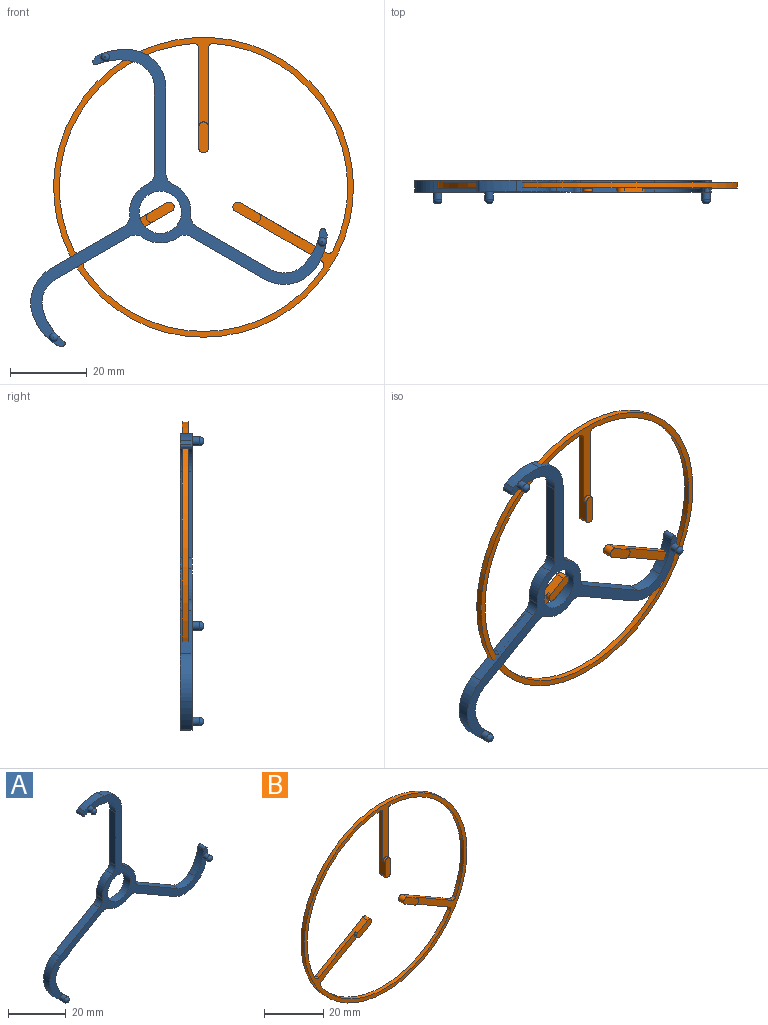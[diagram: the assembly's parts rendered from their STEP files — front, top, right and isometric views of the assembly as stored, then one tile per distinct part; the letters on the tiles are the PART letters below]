
ASSEMBLY  parts=2 mates=1
PART A: 48 faces, bbox 77.2x6x77.2 mm
  f0: plane 3.69x2.41mm, normal (0,-1,0), area 4.6mm2, adj f12,f13,f14,f25,f43
  f1: plane 76.92x75.78mm, normal (0,-1,0), area 488.1mm2, adj f3,f4,f5,f6,f8,f9,f10,f11
  f2: plane 3.75x3.07mm, normal (0,-1,0), area 4.6mm2, adj f6,f7,f8,f26,f41
  f3: plane 22.3x3mm, normal (-1,0,0), area 66.9mm2, adj f1,f23,f30,f33
  f4: cylinder r=8mm len=8.12mm, axis (0,1,0), area 30mm2, adj f1,f23,f33,f38
  f5: plane 19.27x11.13mm, normal (-0.5,0,0.87), area 66.8mm2, adj f1,f23,f29,f38
  f6: cylinder r=16mm len=7.37mm, axis (0,1,0), area 29.4mm2, adj f1,f2,f7,f23,f29
  f7: plane 3x1.13mm, normal (-0.13,0,-0.99), area 3.4mm2, adj f2,f6,f23,f26
  f8: cylinder r=15mm len=8.27mm, axis (0,1,0), area 30.4mm2, adj f1,f2,f23,f26,f32
  f9: plane 19.32x11.15mm, normal (0.5,0,-0.87), area 66.9mm2, adj f1,f23,f32,f37
  f10: cylinder r=8mm len=9.37mm, axis (0,1,0), area 30mm2, adj f1,f23,f36,f37
  f11: plane 19.27x11.13mm, normal (-0.5,0,-0.87), area 66.8mm2, adj f1,f23,f28,f36
  f12: cylinder r=16mm len=9.08mm, axis (0,1,0), area 29.4mm2, adj f0,f1,f13,f23,f28
  f13: plane 3x1.06mm, normal (0.92,0,0.38), area 3.4mm2, adj f0,f12,f23,f25
  f14: cylinder r=15mm len=8.91mm, axis (0,1,0), area 30.4mm2, adj f0,f1,f23,f25,f31
  f15: plane 19.32x11.15mm, normal (0.5,0,0.87), area 66.9mm2, adj f1,f23,f31,f35
  f16: cylinder r=8mm len=8.12mm, axis (0,1,0), area 30mm2, adj f1,f23,f34,f35
  f17: plane 22.26x3mm, normal (1,0,0), area 66.8mm2, adj f1,f23,f27,f34
  f18: cylinder r=16mm len=9.49mm, axis (0,1,0), area 29.4mm2, adj f1,f19,f22,f23,f27
  f19: plane 3x0.91mm, normal (-0.79,0,0.61), area 3.4mm2, adj f18,f22,f23,f24
  f20: cylinder r=15mm len=9.92mm, axis (0,1,0), area 30.4mm2, adj f1,f22,f23,f24,f30
  f21: cylinder r=5.5mm len=11mm, axis (0,1,0), area 103.7mm2, adj f1,f23
  f22: plane 3.49x3mm, normal (0,-1,0), area 4.6mm2, adj f18,f19,f20,f24,f39
  f23: plane 77.23x77.15mm, normal (0,1,0), area 513.6mm2, adj f3,f4,f5,f6,f7,f8,f9,f10
  f24: cylinder r=0.75mm len=3mm, axis (0,1,0), area 5.9mm2, adj f19,f20,f22,f23
  f25: cylinder r=0.75mm len=3mm, axis (0,1,0), area 5.9mm2, adj f0,f13,f14,f23
  f26: cylinder r=0.75mm len=3mm, axis (0,1,0), area 5.9mm2, adj f2,f7,f8,f23
  f27: cylinder r=10mm len=9.92mm, axis (0,1,0), area 43.3mm2, adj f1,f17,f18,f23
  f28: cylinder r=10mm len=12.95mm, axis (0,1,0), area 43.3mm2, adj f1,f11,f12,f23
  f29: cylinder r=10mm len=12.52mm, axis (0,1,0), area 43.3mm2, adj f1,f5,f6,f23
  f30: cylinder r=7mm len=6.74mm, axis (0,1,0), area 27.2mm2, adj f1,f3,f20,f23
  f31: cylinder r=7mm len=8.39mm, axis (0,1,0), area 27.2mm2, adj f1,f14,f15,f23
  f32: cylinder r=7mm len=7.79mm, axis (0,1,0), area 27.2mm2, adj f1,f8,f9,f23
  f33: cylinder r=3mm len=3mm, axis (0,1,0), area 10.3mm2, adj f1,f3,f4,f23
  f34: cylinder r=3mm len=3mm, axis (0,1,0), area 10.3mm2, adj f1,f16,f17,f23
  f35: cylinder r=3mm len=3mm, axis (0,1,0), area 10.3mm2, adj f1,f15,f16,f23
  f36: cylinder r=3mm len=3.26mm, axis (0,1,0), area 10.3mm2, adj f1,f10,f11,f23
  f37: cylinder r=3mm len=3.26mm, axis (0,1,0), area 10.3mm2, adj f1,f9,f10,f23
  f38: cylinder r=3mm len=3mm, axis (0,1,0), area 10.3mm2, adj f1,f4,f5,f23
  f39: cylinder r=1.12mm len=2.24mm, axis (0,1,0), area 14.1mm2, adj f1,f22,f47
  f40: plane 0.24x0.24mm, normal (0,-1,0), area 0mm2, adj f47
  f41: cylinder r=1.12mm len=2.24mm, axis (0,1,0), area 14.1mm2, adj f1,f2,f46
  f42: plane 0.24x0.24mm, normal (0,-1,0), area 0mm2, adj f46
  f43: cylinder r=1.12mm len=2.24mm, axis (0,1,0), area 14.1mm2, adj f0,f1,f45
  f44: plane 0.24x0.24mm, normal (0,-1,0), area 0mm2, adj f45
  f45: torus R=0.12mm, axis (0,-1,0), area 7.4mm2, adj f43,f44
  f46: torus R=0.12mm, axis (0,-1,0), area 7.4mm2, adj f41,f42
  f47: torus R=0.12mm, axis (0,-1,0), area 7.4mm2, adj f39,f40
PART B: 27 faces, bbox 78x2.5x78 mm
  f0: cylinder r=37.5mm len=53.88mm, axis (0,1,0), area 110mm2, adj f10,f11,f21,f26
  f1: plane 22.44x12.96mm, normal (0.5,0,0.87), area 44.4mm2, adj f10,f11,f14,f15,f16,f21
  f2: plane 22.44x12.96mm, normal (-0.5,0,-0.87), area 44.4mm2, adj f10,f11,f14,f15,f16,f22
  f3: cylinder r=37.5mm len=62.21mm, axis (0,1,0), area 110mm2, adj f10,f11,f22,f23
  f4: plane 22.44x12.96mm, normal (0.5,0,-0.87), area 44.4mm2, adj f10,f11,f13,f17,f18,f23
  f5: plane 22.44x12.96mm, normal (-0.5,0,0.87), area 44.4mm2, adj f10,f11,f13,f17,f18,f24
  f6: cylinder r=37.5mm len=53.88mm, axis (0,1,0), area 110mm2, adj f10,f11,f24,f25
  f7: plane 25.91x2.5mm, normal (-1,0,0), area 44.4mm2, adj f10,f11,f12,f19,f20,f25
  f8: plane 25.91x2.5mm, normal (1,0,0), area 44.4mm2, adj f10,f11,f12,f19,f20,f26
  f9: cylinder r=39mm len=78mm, axis (0,1,0), area 367.6mm2, adj f10,f11
  f10: plane 78x78mm, normal (0,-1,0), area 518.5mm2, adj f0,f1,f2,f3,f4,f5,f6,f7
  f11: plane 78x78mm, normal (0,1,0), area 574.5mm2, adj f0,f1,f2,f3,f4,f5,f6,f7
  f12: plane 8x2.5mm, normal (0,-1,0), area 18.7mm2, adj f7,f8,f19,f20
  f13: plane 7.26x5.25mm, normal (0,-1,0), area 18.7mm2, adj f4,f5,f17,f18
  f14: plane 7.26x5.25mm, normal (0,-1,0), area 18.7mm2, adj f1,f2,f15,f16
  f15: cylinder r=1.25mm len=2.33mm, axis (0,-1,0), area 3.9mm2, adj f1,f2,f10,f14
  f16: cylinder r=1.25mm len=2.5mm, axis (0,-1,0), area 9.8mm2, adj f1,f2,f11,f14
  f17: cylinder r=1.25mm len=2.33mm, axis (0,-1,0), area 3.9mm2, adj f4,f5,f10,f13
  f18: cylinder r=1.25mm len=2.5mm, axis (0,-1,0), area 9.8mm2, adj f4,f5,f11,f13
  f19: cylinder r=1.25mm len=2.5mm, axis (0,-1,0), area 3.9mm2, adj f7,f8,f10,f12
  f20: cylinder r=1.25mm len=2.5mm, axis (0,-1,0), area 9.8mm2, adj f7,f8,f11,f12
  f21: cylinder r=1.25mm len=1.75mm, axis (0,1,0), area 3.1mm2, adj f0,f1,f10,f11
  f22: cylinder r=1.25mm len=1.78mm, axis (0,1,0), area 3.1mm2, adj f2,f3,f10,f11
  f23: cylinder r=1.25mm len=1.78mm, axis (0,1,0), area 3.1mm2, adj f3,f4,f10,f11
  f24: cylinder r=1.25mm len=1.75mm, axis (0,1,0), area 3.1mm2, adj f5,f6,f10,f11
  f25: cylinder r=1.25mm len=1.5mm, axis (0,1,0), area 3.1mm2, adj f6,f7,f10,f11
  f26: cylinder r=1.25mm len=1.5mm, axis (0,1,0), area 3.1mm2, adj f0,f8,f10,f11
PLACE A t=(-21.94,-5.69,-1.97)mm
PLACE B t=(-10.68,-6.19,4.53)mm
MATE fastened B.f13 <-> A.f10  axis (0,-1,0) through (-21.94,-8.69,-1.97)mm
